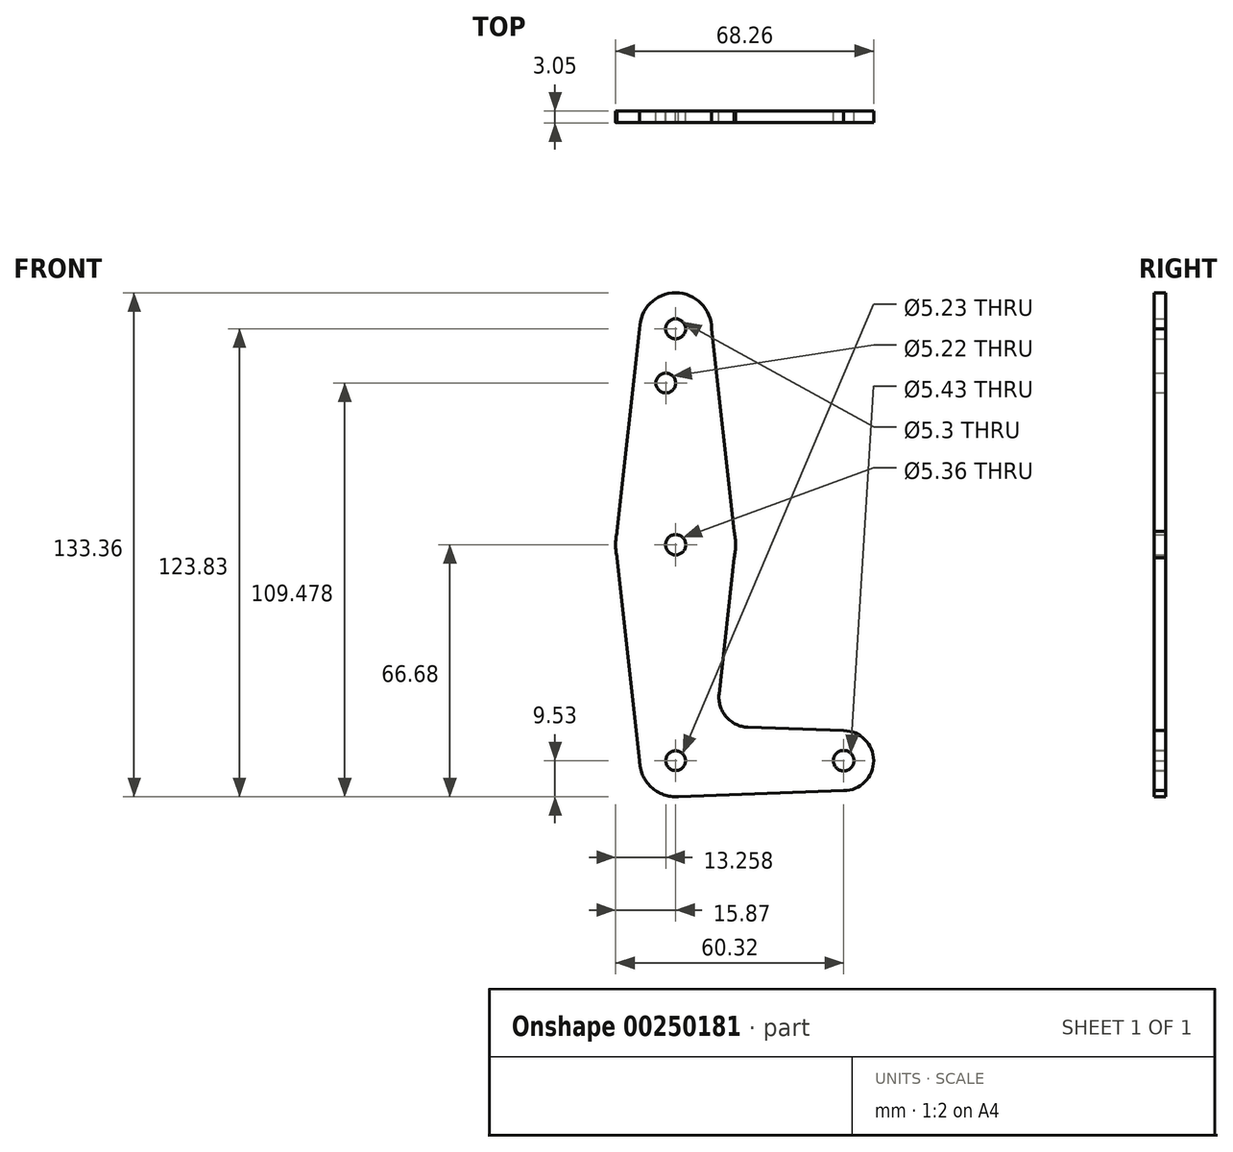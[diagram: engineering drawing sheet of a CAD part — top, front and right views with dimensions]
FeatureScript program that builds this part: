
annotation { "Feature Type Name" : "Feature", "Feature Type Description" : "" }
export const myFeature = defineFeature(function(context is Context, id is Id, definition is map)
    precondition{}
    {
        {
            var Q0;
            Q0=qCreatedBy(makeId("Front.planeOp"),FACE);
            var sketch = newSketch(context, id + "F0", { "sketchPlane" : qUnion([Q0])});
            skLineSegment(sketch, "E0", {"start": v(0, 114.3) * mm, "end": v(0, 0) * mm, "construction": true});
            skCircle(sketch, "E1", {"center": v(0, 114.3) * mm, "radius": 9.53 * mm});
            skCircle(sketch, "E2", {"center": v(0, 57.15) * mm, "radius": 15.88 * mm});
            skCircle(sketch, "E3", {"center": v(0, 0) * mm, "radius": 9.52 * mm});
            skLineSegment(sketch, "E4", {"start": v(0, 0) * mm, "end": v(44.45, 0) * mm, "construction": true});
            skCircle(sketch, "E5", {"center": v(44.45, 0) * mm, "radius": 7.94 * mm});
            skLineSegment(sketch, "E6", {"start": v(9.53, 114.3) * mm, "end": v(15.88, 57.15) * mm});
            skLineSegment(sketch, "E7", {"start": v(-9.52, 114.3) * mm, "end": v(-15.87, 57.15) * mm});
            skLineSegment(sketch, "E8", {"start": v(-15.87, 57.15) * mm, "end": v(-9.52, 0) * mm});
            skLineSegment(sketch, "E9", {"start": v(15.88, 57.15) * mm, "end": v(11.49, 17.67) * mm});
            skLineSegment(sketch, "E10", {"start": v(0, -9.52) * mm, "end": v(44.45, -7.94) * mm});
            skLineSegment(sketch, "E11", {"start": v(19.1, 8.84) * mm, "end": v(44.45, 7.94) * mm});
            skArc(sketch, "E12.filletArc", {"start": v(11.49, 17.67) * mm, "mid": v(13.37, 11.6) * mm, "end": v(19.1, 8.84) * mm});
            skCircle(sketch, "E13", {"center": v(-2.61, 99.95) * mm, "radius": 2.61 * mm});
            skCircle(sketch, "E14", {"center": v(0, 114.3) * mm, "radius": 2.65 * mm});
            skCircle(sketch, "E15", {"center": v(0, 57.15) * mm, "radius": 2.68 * mm});
            skCircle(sketch, "E16", {"center": v(0, 0) * mm, "radius": 2.61 * mm});
            skCircle(sketch, "E17", {"center": v(44.45, 0) * mm, "radius": 2.72 * mm});
            skSolve(sketch);
        }
        {
            var Q0;
            Q0 = qSketchRegion(id + "F0", true);
            extrude(context, id + "F1", {"entities" : qUnion([Q0]), "depth" : 3.05 * mm});
        }
    });
